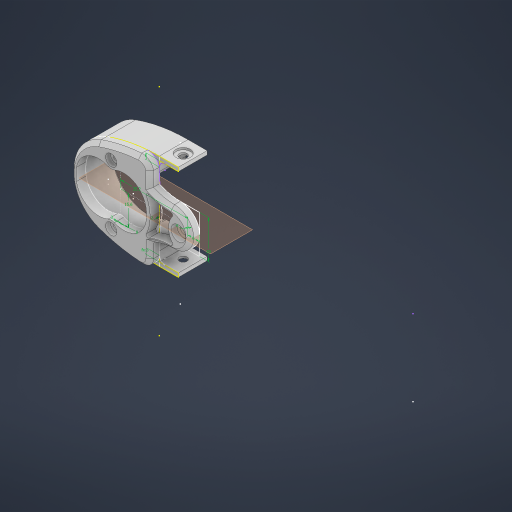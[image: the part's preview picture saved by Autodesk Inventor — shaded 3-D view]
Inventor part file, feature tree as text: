
AUTODESK INVENTOR PART (.ipt)
format: ipt  version: 2024.2 (Build 282272000, 272)  size: 844,800 bytes
history: native  units: in
note: dims shown in document units (in); Inventor stores cm internally (conversion verified against a paired STEP export)
features: extrude x8, sketch x8, projected_geometry x5, mirror x2, chamfer x2, plane x1, fillet x1
ambient origin geometry x8: Origin, YZ Plane, XZ Plane, XY Plane, X Axis, Y Axis, Z Axis, Center Point
bodies: Solid1 (feature_tree)
feature tree (27):
  extrude  "Extrusion1"  Depth=1.9685in
  plane  "Work Plane1"
  sketch  "Sketch2"  dims[d3=0.0787in d4=1.6929in]
  extrude  "Extrusion2"  Depth=0.0787in
  extrude  "Extrusion4"  Depth=0.1181in
  mirror  "Mirror2"
  extrude  "Extrusion5"  Depth=0.315in
  extrude  "Extrusion7"  Depth=1.3858in
  extrude  "Extrusion8"  Depth=0.7874in
  mirror  "Mirror4"
  chamfer  "Chamfer1"  Distance=0.1969in
  extrude  "Extrusion11"  Depth=0.0984in TaperAngle=0.0deg
  fillet  "Fillet3"  Radius=0.1181in
  chamfer  "Chamfer4"  Distance=0.1181in
  extrude  "Extrusion12"  Depth=0.0787in
  sketch  "Sketch1"  dims[d0=1.4567in d2=1.9685in]
  projected_geometry  "Projected Loop1"
  sketch  "Sketch3"  dims[d6=0.5906in d7=0.0in d8=0.1181in]
  projected_geometry  "Projected Loop2"
  sketch  "Sketch4"  dims[d9=0.6142in d10=0.315in]
  projected_geometry  "Projected Loop3"
  sketch  "Sketch5"  dims[d11=0.0787in d12=1.3858in]
  projected_geometry  "Projected Loop4"
  sketch  "Sketch6"  dims[d13=0.1575in d14=0.7874in]
  projected_geometry  "Projected Loop5"
  sketch  "Sketch9"  dims[d15=0.2362in d16=0.1969in d17=0.0in]
  sketch  "Sketch10"  dims[d20=0.2323in d21=0.0984in d22=0.0in d23=0.1181in d24=0.1181in d25=0.0787in d26=0.1575in d28=0.3937in d30=0.7087in d32=0.1969in d33=0.0in d36=0.1575in d37=0.1969in d38=0.0in d39=0.0in d40=0.2953in d41=0.0394in d42=0.0in d45=0.0787in d46=0.0787in d47=45.0deg d52=0.7953in d53=0.3937in d62=0.2756in d63=0.8661in d64=0.3937in d65=0.0in d66=0.0787in d67=0.0394in d68=0.0787in d69=45.0deg d70=0.3031in d71=0.1181in d72=0.0in d54=0.0197in d55=0.0344in d56=0.0197in d57=0.0344in]
